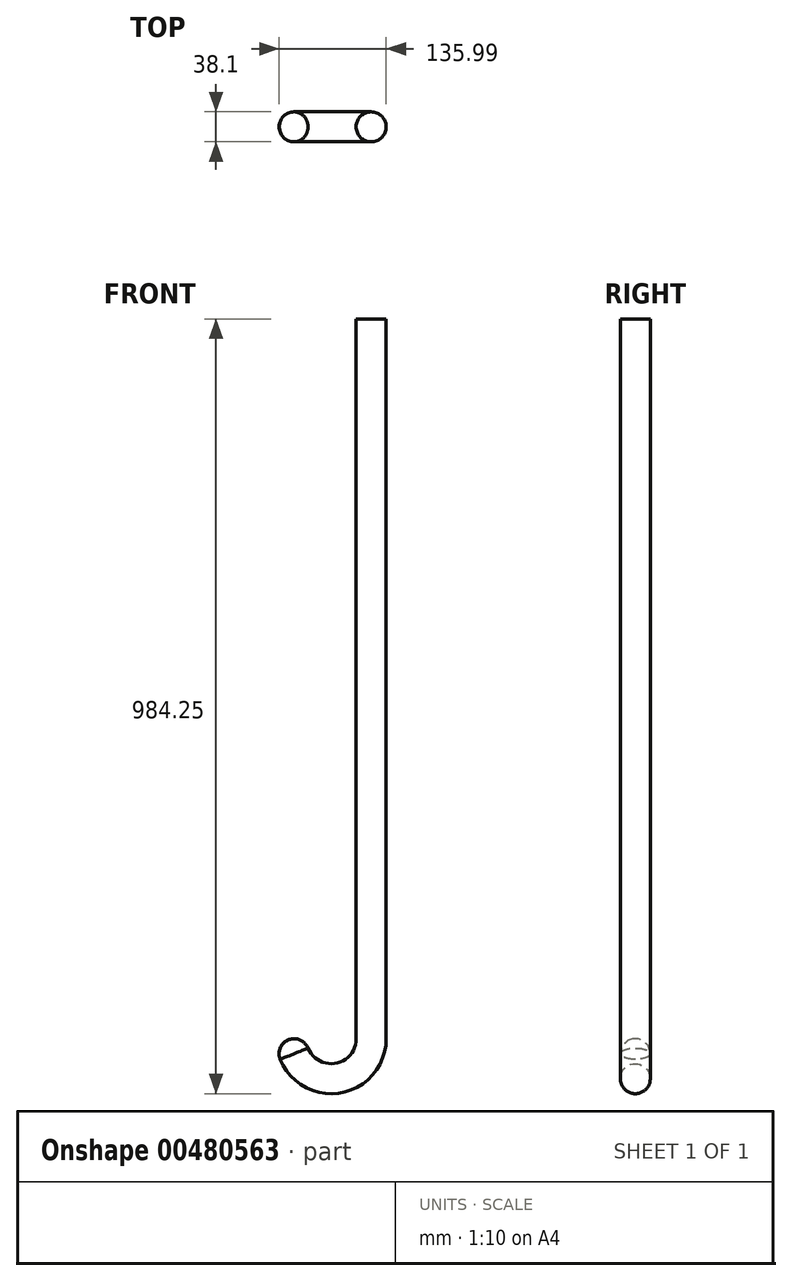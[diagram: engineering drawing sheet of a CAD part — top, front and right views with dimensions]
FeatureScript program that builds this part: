
annotation { "Feature Type Name" : "Feature", "Feature Type Description" : "" }
export const myFeature = defineFeature(function(context is Context, id is Id, definition is map)
    precondition{}
    {
        {
            var Q0;
            Q0=qCreatedBy(makeId("Top.planeOp"),FACE);
            cPlane(context, id + "F0", {"entities" : qUnion([Q0]), "cplaneType" : CPlaneType.OFFSET, "offset" : 381 * mm, "width" : 152.4 * mm, "height" : 152.4 * mm});
        }
        {
            var Q0;
            Q0=qCreatedBy(id+"F0.planeOp",FACE);
            var sketch = newSketch(context, id + "F1", { "sketchPlane" : qUnion([Q0])});
            skCircle(sketch, "E0", {"center": v(0, 0) * mm, "radius": 76.2 * mm});
            skLineSegment(sketch, "E1", {"start": v(0, 76.2) * mm, "end": v(0, -76.2) * mm, "construction": true});
            skLineSegment(sketch, "E2.1.0", {"start": v(53.88, 53.88) * mm, "end": v(-53.88, -53.88) * mm, "construction": true});
            skLineSegment(sketch, "E2.2.0", {"start": v(76.2, 0) * mm, "end": v(-76.2, 0) * mm, "construction": true});
            skLineSegment(sketch, "E2.3.0", {"start": v(53.88, -53.88) * mm, "end": v(-53.88, 53.88) * mm, "construction": true});
            skLineSegment(sketch, "E2.anchor1", {"start": v(0, 0) * mm, "end": v(0, -76.2) * mm, "construction": true});
            skLineSegment(sketch, "E2.anchor2", {"start": v(0, 0) * mm, "end": v(-53.88, 53.88) * mm, "construction": true});
            skSolve(sketch);
        }
        {
            var Q0;
            Q0=qCreatedBy(makeId("Front.planeOp"),FACE);
            var sketch = newSketch(context, id + "F2", { "sketchPlane" : qUnion([Q0])});
            skLineSegment(sketch, "E3", {"start": v(0, 0) * mm, "end": v(0, 381) * mm, "construction": true});
            skSolve(sketch);
        }
        {
            var Q0;
            Q0=qCreatedBy(makeId("Top.planeOp"),FACE);
            var sketch = newSketch(context, id + "F3", { "sketchPlane" : qUnion([Q0])});
            skCircle(sketch, "E4.cCircle", {"center": v(0, 0) * mm, "radius": 422.4 * mm, "construction": true});
            skLineSegment(sketch, "E4.0", {"start": v(323.29, 323.29) * mm, "end": v(457.2, 0) * mm});
            skLineSegment(sketch, "E4.1", {"start": v(457.2, 0) * mm, "end": v(323.29, -323.29) * mm});
            skLineSegment(sketch, "E4.2", {"start": v(323.29, -323.29) * mm, "end": v(0, -457.2) * mm});
            skLineSegment(sketch, "E4.3", {"start": v(0, -457.2) * mm, "end": v(-323.29, -323.29) * mm});
            skLineSegment(sketch, "E4.4", {"start": v(-323.29, -323.29) * mm, "end": v(-457.2, 0) * mm});
            skLineSegment(sketch, "E4.5", {"start": v(-457.2, 0) * mm, "end": v(-323.29, 323.29) * mm});
            skLineSegment(sketch, "E4.6", {"start": v(-323.29, 323.29) * mm, "end": v(0, 457.2) * mm});
            skLineSegment(sketch, "E4.7", {"start": v(0, 457.2) * mm, "end": v(323.29, 323.29) * mm});
            skPoint(sketch, "E4.0.midPoint", {"position": v(390.24, 161.64) * mm});
            skLineSegment(sketch, "E5", {"start": v(0, 457.2) * mm, "end": v(0, -457.2) * mm, "construction": true});
            skSolve(sketch);
        }
        {
            var Q0;
            Q0=qCreatedBy(makeId("Front.planeOp"),FACE);
            var sketch = newSketch(context, id + "F4", { "sketchPlane" : qUnion([Q0])});
            skArc(sketch, "E6", {"start": v(457.2, 0) * mm, "mid": v(345.6, 269.4) * mm, "end": v(76.2, 381) * mm});
            skArc(sketch, "E7.MirrorCS", {"start": v(-457.2, 0) * mm, "mid": v(-345.6, 269.4) * mm, "end": v(-76.2, 381) * mm});
            skSolve(sketch);
        }
        {
            var Q0;
            Q0=qCreatedBy(makeId("Front.planeOp"),FACE);
            var Q1;
            Q1=sQuery(id+"F2.wireOp",EDGE,"E3");
            cPlane(context, id + "F5", {"entities" : qUnion([Q0, Q1]), "cplaneType" : CPlaneType.LINE_ANGLE, "offset" : 25.4 * mm, "angle" : 45 * degree, "width" : 152.4 * mm, "height" : 152.4 * mm});
        }
        {
            var Q0;
            Q0=qCreatedBy(id+"F5.planeOp",FACE);
            var sketch = newSketch(context, id + "F6", { "sketchPlane" : qUnion([Q0])});
            skArc(sketch, "E8", {"start": v(-76.2, 381) * mm, "mid": v(-345.6, 269.4) * mm, "end": v(-457.2, 0) * mm});
            skArc(sketch, "E9.MirrorCS", {"start": v(76.2, 381) * mm, "mid": v(345.6, 269.4) * mm, "end": v(457.2, 0) * mm});
            skSolve(sketch);
        }
        {
            var Q0;
            Q0=qCreatedBy(makeId("Front.planeOp"),FACE);
            var sketch = newSketch(context, id + "F7", { "sketchPlane" : qUnion([Q0])});
            skLineSegment(sketch, "E10", {"start": v(0, 381) * mm, "end": v(0, -533.4) * mm});
            skArc(sketch, "E11", {"start": v(-101.6, -533.4) * mm, "mid": v(-50.8, -584.2) * mm, "end": v(0, -533.4) * mm});
            skSolve(sketch);
        }
        {
            var Q0;
            Q0=qCreatedBy(id+"F0.planeOp",FACE);
            var sketch = newSketch(context, id + "F8", { "sketchPlane" : qUnion([Q0])});
            skCircle(sketch, "E12", {"center": v(0, 0) * mm, "radius": 19.05 * mm});
            skSolve(sketch);
        }
        {
            var Q0;
            Q0=makeQuery(id+"F3.imprint","IMPRINT",FACE,{"disambiguationData":[TD([[makeQuery(id+"F3.imprint","IMPRINT",EDGE,{"derivedFrom":sQuery(id+"F3.wireOp",EDGE,"E4.0")}),-1.0]])]});
            var Q1;
            Q1=sQuery(id+"F1.wireOp",EDGE,"E0");
            var Q2;
            Q2=sQuery(id+"FwEUsNg9eqqxYRy_0.1.F6.wireOp",EDGE,"E9.MirrorCS");
            var Q3;
            Q3=sQuery(id+"FwEUsNg9eqqxYRy_0.1.F4.wireOp",EDGE,"E7.MirrorCS");
            var Q4;
            Q4=sQuery(id+"F6.wireOp",EDGE,"E9.MirrorCS");
            var Q5;
            Q5=sQuery(id+"F4.wireOp",EDGE,"E7.MirrorCS");
            var Q6;
            Q6=sQuery(id+"FwEUsNg9eqqxYRy_0.1.F6.wireOp",EDGE,"E8");
            var Q7;
            Q7=sQuery(id+"FwEUsNg9eqqxYRy_0.1.F4.wireOp",EDGE,"E6");
            var Q8;
            Q8=sQuery(id+"F6.wireOp",EDGE,"E8");
            var Q9;
            Q9=sQuery(id+"F4.wireOp",EDGE,"E6");
            loft(context, id + "F9", {"bodyType" : ToolBodyType.SURFACE, "addGuides" : true, "wireProfilesArray" : [{ "wireProfileEntities" : qUnion([Q0]) }, { "wireProfileEntities" : qUnion([Q1]) }], "guidesArray" : [{ "guideEntities" : qUnion([Q2]), "guideDerivativeType" : LoftGuideDerivativeType.DEFAULT, "guideDerivativeMagnitude" : 1 }, { "guideEntities" : qUnion([Q3]), "guideDerivativeType" : LoftGuideDerivativeType.DEFAULT, "guideDerivativeMagnitude" : 1 }, { "guideEntities" : qUnion([Q4]), "guideDerivativeType" : LoftGuideDerivativeType.DEFAULT, "guideDerivativeMagnitude" : 1 }, { "guideEntities" : qUnion([Q5]), "guideDerivativeType" : LoftGuideDerivativeType.DEFAULT, "guideDerivativeMagnitude" : 1 }, { "guideEntities" : qUnion([Q6]), "guideDerivativeType" : LoftGuideDerivativeType.DEFAULT, "guideDerivativeMagnitude" : 1 }, { "guideEntities" : qUnion([Q7]), "guideDerivativeType" : LoftGuideDerivativeType.DEFAULT, "guideDerivativeMagnitude" : 1 }, { "guideEntities" : qUnion([Q8]), "guideDerivativeType" : LoftGuideDerivativeType.DEFAULT, "guideDerivativeMagnitude" : 1 }, { "guideEntities" : qUnion([Q9]), "guideDerivativeType" : LoftGuideDerivativeType.DEFAULT, "guideDerivativeMagnitude" : 1 }]});
        }
        {
            var Q0;
            Q0=makeQuery(id+"F8.imprint","IMPRINT",FACE,{"disambiguationData":[TD([[makeQuery(id+"F8.imprint","IMPRINT",EDGE,{"derivedFrom":sQuery(id+"F8.wireOp",EDGE,"E12")}),1.0]])]});
            var Q1;
            Q1=sQuery(id+"F7.wireOp",EDGE,"E10");
            var Q2;
            Q2=sQuery(id+"F7.wireOp",EDGE,"E11");
            sweep(context, id + "F10", {"profiles" : qUnion([Q0]), "path" : qUnion([Q1, Q2])});
        }
        {
            var Q0;
            Q0=makeQuery(id+"F10.opSweep","CAP_EDGE",EDGE,{"disambiguationData":[OSD([sQuery(id+"F7.wireOp",VERTEX,"E11.start"),sQuery(id+"F8.wireOp",EDGE,"E12")])],"isStart":false});
            fillet(context, id + "F11", {"entities" : qUnion([Q0]), "radius" : 19.05 * mm, "tangentPropagation" : true, "allowEdgeOverflow" : false});
        }
    });
